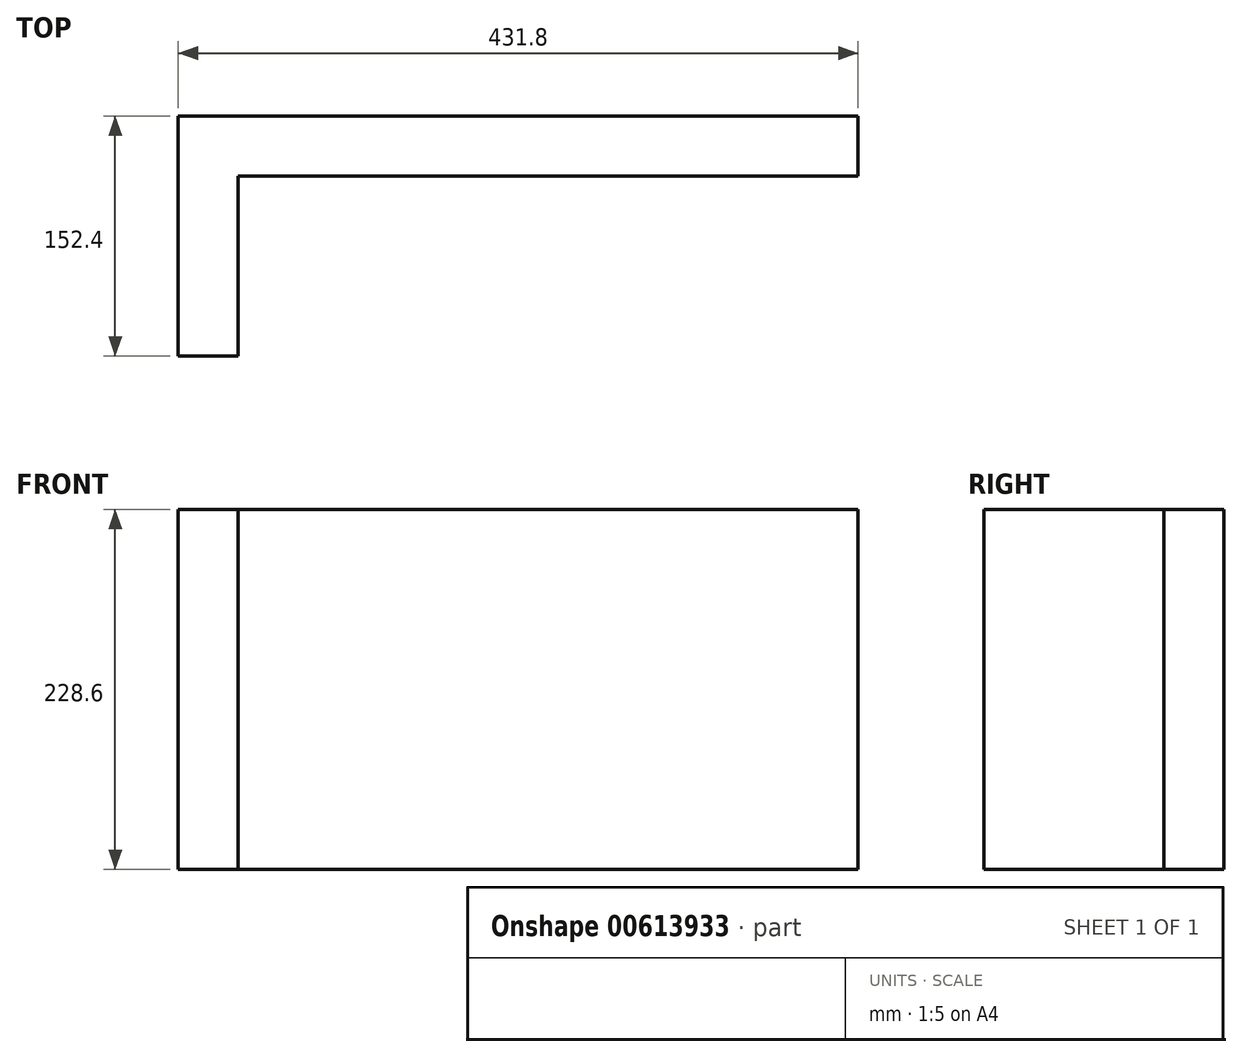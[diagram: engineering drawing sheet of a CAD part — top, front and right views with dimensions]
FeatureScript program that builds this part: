
annotation { "Feature Type Name" : "Feature", "Feature Type Description" : "" }
export const myFeature = defineFeature(function(context is Context, id is Id, definition is map)
    precondition{}
    {
        {
            var Q0;
            Q0=qCreatedBy(makeId("Top.planeOp"),FACE);
            var sketch = newSketch(context, id + "F0", { "sketchPlane" : qUnion([Q0])});
            skLineSegment(sketch, "E0.bottom", {"start": v(-143.56, 33.45) * mm, "end": v(288.24, 33.45) * mm});
            skLineSegment(sketch, "E0.top", {"start": v(-105.46, -4.65) * mm, "end": v(288.24, -4.65) * mm});
            skLineSegment(sketch, "E0.left", {"start": v(-143.56, 33.45) * mm, "end": v(-143.56, -4.65) * mm});
            skLineSegment(sketch, "E0.right", {"start": v(288.24, 33.45) * mm, "end": v(288.24, -4.65) * mm});
            skLineSegment(sketch, "E1.bottom", {"start": v(-143.56, 33.45) * mm, "end": v(-105.46, 33.45) * mm});
            skLineSegment(sketch, "E1.top", {"start": v(-143.56, -118.95) * mm, "end": v(-105.46, -118.95) * mm});
            skLineSegment(sketch, "E1.left", {"start": v(-143.56, 33.45) * mm, "end": v(-143.56, -118.95) * mm});
            skLineSegment(sketch, "E1.right", {"start": v(-105.46, -4.65) * mm, "end": v(-105.46, -118.95) * mm});
            skSolve(sketch);
        }
        {
            var Q0;
            Q0 = qSketchRegion(id + "F0", true);
            extrude(context, id + "F1", {"entities" : qUnion([Q0]), "depth" : 228.6 * mm, "offsetDistance" : 25.4 * mm});
        }
    });
